# Revit family: Door-Exterior_Interior-Simpson-French-Full_Glass-Half_Arch-Single
name_source: partatom
category: Doors
revit_build: Autodesk Revit Architecture 2012 (Build: 20110916_2132(x64)
units: mm (PartAtom-declared; Revit-internal decimal feet)

## types (231) — shared parameters
Arch Bottom Height = 0' - 9 13/32"
Assembly Code = B2030230
Bottom Rail Height = 0' - 8 13/16"
Construction Type = Wood
Frame = Wood - Simpson Doors - Douglas Fir
Frame Projection Ext. = 0' - 1"
Frame Projection Int. = 0' - 1"
Frame Type = Frame : Standard
Frame Width = 0' - 3"
Function = Exterior
Glass = Glass - Simpson Doors - Clear
Glass Options = http://simpsondoor.com
Manufacturer = Simpsons Door Company
Middle Rail Height = 0' - 6 3/4"
Muntin Width = 0' - 0 1/2"
Ovolo Construction = Yes
Panel = Wood - Simpson Doors - Douglas Fir
Panel Stile Width = 0' - 4 1/8"
Product Documentation Link = http://www.simpsondoor.com
Product Page URL = http://www.simpsondoor.com
Thickness = 0' - 1 3/4"
Thickness Note = comes in 1 3/4" and 2 1/4" Thickness. Default is set to 1 3/4"
Top Rail Height = 0' - 4 1/32"
URL = http://www.simpsondoor.com
UltraBlock Note = This Door Comes with The Option of UltraBlock Technology. It is Turn On as a Default
UltraBlock Option = Yes
Wall Closure = By host
WaterBarrier Note = This Door Comes with The Option of WaterBarrier with UltraBlock Technology. It is Turn Off as a Default
WaterBarrier with UltraBlock Technology = No
Wood Species = http://simpsondoor.com
Wood Species Note = Available in Any Wood Species

## per-type parameters (varying)
| type | Description | Height | Model | Number of Horizontal Muntins | Number of Vertical Muntins | Rough Height | Rough Width | Width |
| 1420-1430 Exterior French 30x80 Ovolo Flat Panel | Exterior French - Ten Lite | 6' - 8" | 1420-1430 | 4 | 1 | 6' - 10" | 2' - 10" | 2' - 6" |
| 1420-1430 Exterior French 30x84 Ovolo Flat Panel | Exterior French - Ten Lite | 7' - 0" | 1420-1430 | 4 | 1 | 7' - 2" | 2' - 10" | 2' - 6" |
| 1420-1430 Exterior French 30x96 Ovolo Flat Panel | Exterior French - Ten Lite | 8' - 0" | 1420-1430 | 4 | 1 | 8' - 2" | 2' - 10" | 2' - 6" |
| 1420-1430 Exterior French 32x80 Ovolo Flat Panel | Exterior French - Ten Lite | 6' - 8" | 1420-1430 | 4 | 1 | 6' - 10" | 3' - 0" | 2' - 8" |
| 1420-1430 Exterior French 32x84 Ovolo Flat Panel | Exterior French - Ten Lite | 7' - 0" | 1420-1430 | 4 | 1 | 7' - 2" | 3' - 0" | 2' - 8" |
| 1420-1430 Exterior French 32x96 Ovolo Flat Panel | Exterior French - Ten Lite | 8' - 0" | 1420-1430 | 4 | 1 | 8' - 2" | 3' - 0" | 2' - 8" |
| 1420-1430 Exterior French 34x80 Ovolo Flat Panel | Exterior French - Ten Lite | 6' - 8" | 1420-1430 | 4 | 1 | 6' - 10" | 3' - 2" | 2' - 10" |
| 1420-1430 Exterior French 34x84 Ovolo Flat Panel | Exterior French - Ten Lite | 7' - 0" | 1420-1430 | 4 | 1 | 7' - 2" | 3' - 2" | 2' - 10" |
| 1420-1430 Exterior French 34x96 Ovolo Flat Panel | Exterior French - Ten Lite | 8' - 0" | 1420-1430 | 4 | 1 | 8' - 2" | 3' - 2" | 2' - 10" |
| 1420-1430 Exterior French 36x80 Ovolo Flat Panel | Exterior French - Ten Lite | 6' - 8" | 1420-1430 | 4 | 1 | 6' - 10" | 3' - 4" | 3' - 0" |
| 1420-1430 Exterior French 36x84 Ovolo Flat Panel | Exterior French - Ten Lite | 7' - 0" | 1420-1430 | 4 | 1 | 7' - 2" | 3' - 4" | 3' - 0" |
| 1420-1430 Exterior French 36x96 Ovolo Flat Panel | Exterior French - Ten Lite | 8' - 0" | 1420-1430 | 4 | 1 | 8' - 2" | 3' - 4" | 3' - 0" |
| 1420-1430 Exterior French 38x80 Ovolo Flat Panel | Exterior French - Ten Lite | 6' - 8" | 1420-1430 | 4 | 1 | 6' - 10" | 3' - 6" | 3' - 2" |
| 1420-1430 Exterior French 38x84 Ovolo Flat Panel | Exterior French - Ten Lite | 7' - 0" | 1420-1430 | 4 | 1 | 7' - 2" | 3' - 6" | 3' - 2" |
| 1420-1430 Exterior French 38x96 Ovolo Flat Panel | Exterior French - Ten Lite | 8' - 0" | 1420-1430 | 4 | 1 | 8' - 2" | 3' - 6" | 3' - 2" |
| 1420-1430 Exterior French 40x80 Ovolo Flat Panel | Exterior French - Ten Lite | 6' - 8" | 1420-1430 | 4 | 1 | 6' - 10" | 3' - 8" | 3' - 4" |
| 1420-1430 Exterior French 40x84 Ovolo Flat Panel | Exterior French - Ten Lite | 7' - 0" | 1420-1430 | 4 | 1 | 7' - 2" | 3' - 8" | 3' - 4" |
| 1420-1430 Exterior French 40x96 Ovolo Flat Panel | Exterior French - Ten Lite | 8' - 0" | 1420-1430 | 4 | 1 | 8' - 2" | 3' - 8" | 3' - 4" |
| 1420-1430 Exterior French 42x80 Ovolo Flat Panel | Exterior French - Ten Lite | 6' - 8" | 1420-1430 | 4 | 1 | 6' - 10" | 3' - 10" | 3' - 6" |
| 1420-1430 Exterior French 42x84 Ovolo Flat Panel | Exterior French - Ten Lite | 7' - 0" | 1420-1430 | 4 | 1 | 7' - 2" | 3' - 10" | 3' - 6" |
| 1420-1430 Exterior French 42x96 Ovolo Flat Panel | Exterior French - Ten Lite | 8' - 0" | 1420-1430 | 4 | 1 | 8' - 2" | 3' - 10" | 3' - 6" |
| 1421-1431 Exterior French 30x80 Ovolo Flat Panel | Exterior French - Single Lite | 6' - 8" | 1421-1431 | 0 | 0 | 6' - 10" | 2' - 10" | 2' - 6" |
| 1421-1431 Exterior French 30x84 Ovolo Flat Panel | Exterior French - Single Lite | 7' - 0" | 1421-1431 | 0 | 0 | 7' - 2" | 2' - 10" | 2' - 6" |
| 1421-1431 Exterior French 30x96 Ovolo Flat Panel | Exterior French - Single Lite | 8' - 0" | 1421-1431 | 0 | 0 | 8' - 2" | 2' - 10" | 2' - 6" |
| 1421-1431 Exterior French 32x80 Ovolo Flat Panel | Exterior French - Single Lite | 6' - 8" | 1421-1431 | 0 | 0 | 6' - 10" | 3' - 0" | 2' - 8" |
| 1421-1431 Exterior French 32x84 Ovolo Flat Panel | Exterior French - Single Lite | 7' - 0" | 1421-1431 | 0 | 0 | 7' - 2" | 3' - 0" | 2' - 8" |
| 1421-1431 Exterior French 32x96 Ovolo Flat Panel | Exterior French - Single Lite | 8' - 0" | 1421-1431 | 0 | 0 | 8' - 2" | 3' - 0" | 2' - 8" |
| 1421-1431 Exterior French 34x80 Ovolo Flat Panel | Exterior French - Single Lite | 6' - 8" | 1421-1431 | 0 | 0 | 6' - 10" | 3' - 2" | 2' - 10" |
| 1421-1431 Exterior French 34x84 Ovolo Flat Panel | Exterior French - Single Lite | 7' - 0" | 1421-1431 | 0 | 0 | 7' - 2" | 3' - 2" | 2' - 10" |
| 1421-1431 Exterior French 34x96 Ovolo Flat Panel | Exterior French - Single Lite | 8' - 0" | 1421-1431 | 0 | 0 | 8' - 2" | 3' - 2" | 2' - 10" |
| 1421-1431 Exterior French 36x80 Ovolo Flat Panel | Exterior French - Single Lite | 6' - 8" | 1421-1431 | 0 | 0 | 6' - 10" | 3' - 4" | 3' - 0" |
| 1421-1431 Exterior French 36x84 Ovolo Flat Panel | Exterior French - Single Lite | 7' - 0" | 1421-1431 | 0 | 0 | 7' - 2" | 3' - 4" | 3' - 0" |
| 1421-1431 Exterior French 36x96 Ovolo Flat Panel | Exterior French - Single Lite | 8' - 0" | 1421-1431 | 0 | 0 | 8' - 2" | 3' - 4" | 3' - 0" |
| 1421-1431 Exterior French 38x80 Ovolo Flat Panel | Exterior French - Single Lite | 6' - 8" | 1421-1431 | 0 | 0 | 6' - 10" | 3' - 6" | 3' - 2" |
| 1421-1431 Exterior French 38x84 Ovolo Flat Panel | Exterior French - Single Lite | 7' - 0" | 1421-1431 | 0 | 0 | 7' - 2" | 3' - 6" | 3' - 2" |
| 1421-1431 Exterior French 38x96 Ovolo Flat Panel | Exterior French - Single Lite | 8' - 0" | 1421-1431 | 0 | 0 | 8' - 2" | 3' - 6" | 3' - 2" |
| 1421-1431 Exterior French 40x80 Ovolo Flat Panel | Exterior French - Single Lite | 6' - 8" | 1421-1431 | 0 | 0 | 6' - 10" | 3' - 8" | 3' - 4" |
| 1421-1431 Exterior French 40x84 Ovolo Flat Panel | Exterior French - Single Lite | 7' - 0" | 1421-1431 | 0 | 0 | 7' - 2" | 3' - 8" | 3' - 4" |
| 1421-1431 Exterior French 40x96 Ovolo Flat Panel | Exterior French - Single Lite | 8' - 0" | 1421-1431 | 0 | 0 | 8' - 2" | 3' - 8" | 3' - 4" |
| 1421-1431 Exterior French 42x80 Ovolo Flat Panel | Exterior French - Single Lite | 6' - 8" | 1421-1431 | 0 | 0 | 6' - 10" | 3' - 10" | 3' - 6" |
| 1421-1431 Exterior French 42x84 Ovolo Flat Panel | Exterior French - Single Lite | 7' - 0" | 1421-1431 | 0 | 0 | 7' - 2" | 3' - 10" | 3' - 6" |
| 1421-1431 Exterior French 42x96 Ovolo Flat Panel | Exterior French - Single Lite | 8' - 0" | 1421-1431 | 0 | 0 | 8' - 2" | 3' - 10" | 3' - 6" |
| 1426 -1436 Exterior French 30x80 Ovolo Flat Panel | Exterior French - Six Lite | 6' - 8" | 1426-1436 | 2 | 1 | 6' - 10" | 2' - 10" | 2' - 6" |
| 1426-1436 Exterior French 30x84 Ovolo Flat Panel | Exterior French - Six Lite | 7' - 0" | 1426-1436 | 2 | 1 | 7' - 2" | 2' - 10" | 2' - 6" |
| 1426-1436 Exterior French 30x96 Ovolo Flat Panel | Exterior French - Six Lite | 8' - 0" | 1426-1436 | 2 | 1 | 8' - 2" | 2' - 10" | 2' - 6" |
| 1426-1436 Exterior French 32x80 Ovolo Flat Panel | Exterior French - Six Lite | 6' - 8" | 1426-1436 | 2 | 1 | 6' - 10" | 3' - 0" | 2' - 8" |
| 1426-1436 Exterior French 32x84 Ovolo Flat Panel | Exterior French - Six Lite | 7' - 0" | 1426-1436 | 2 | 1 | 7' - 2" | 3' - 0" | 2' - 8" |
| 1426-1436 Exterior French 32x96 Ovolo Flat Panel | Exterior French - Six Lite | 8' - 0" | 1426-1436 | 2 | 1 | 8' - 2" | 3' - 0" | 2' - 8" |
| 1426-1436 Exterior French 34x80 Ovolo Flat Panel | Exterior French - Six Lite | 6' - 8" | 1426-1436 | 2 | 1 | 6' - 10" | 3' - 2" | 2' - 10" |
| 1426-1436 Exterior French 34x84 Ovolo Flat Panel | Exterior French - Six Lite | 7' - 0" | 1426-1436 | 2 | 1 | 7' - 2" | 3' - 2" | 2' - 10" |
| 1426-1436 Exterior French 34x96 Ovolo Flat Panel | Exterior French - Six Lite | 8' - 0" | 1426-1436 | 2 | 1 | 8' - 2" | 3' - 2" | 2' - 10" |
| 1426-1436 Exterior French 36x80 Ovolo Flat Panel | Exterior French - Six Lite | 6' - 8" | 1426-1436 | 2 | 1 | 6' - 10" | 3' - 4" | 3' - 0" |
| 1426-1436 Exterior French 36x84 Ovolo Flat Panel | Exterior French - Six Lite | 7' - 0" | 1426-1436 | 2 | 1 | 7' - 2" | 3' - 4" | 3' - 0" |
| 1426-1436 Exterior French 36x96 Ovolo Flat Panel | Exterior French - Six Lite | 8' - 0" | 1426-1436 | 2 | 1 | 8' - 2" | 3' - 4" | 3' - 0" |
| 1426-1436 Exterior French 38x80 Ovolo Flat Panel | Exterior French - Six Lite | 6' - 8" | 1426-1436 | 2 | 1 | 6' - 10" | 3' - 6" | 3' - 2" |
| 1426-1436 Exterior French 38x84 Ovolo Flat Panel | Exterior French - Six Lite | 7' - 0" | 1426-1436 | 2 | 1 | 7' - 2" | 3' - 6" | 3' - 2" |
| 1426-1436 Exterior French 38x96 Ovolo Flat Panel | Exterior French - Six Lite | 8' - 0" | 1426-1436 | 2 | 1 | 8' - 2" | 3' - 6" | 3' - 2" |
| 1426-1436 Exterior French 40x80 Ovolo Flat Panel | Exterior French - Six Lite | 6' - 8" | 1426-1436 | 2 | 1 | 6' - 10" | 3' - 8" | 3' - 4" |
| 1426-1436 Exterior French 40x84 Ovolo Flat Panel | Exterior French - Six Lite | 7' - 0" | 1426-1436 | 2 | 1 | 7' - 2" | 3' - 8" | 3' - 4" |
| 1426-1436 Exterior French 40x96 Ovolo Flat Panel | Exterior French - Six Lite | 8' - 0" | 1426-1436 | 2 | 1 | 8' - 2" | 3' - 8" | 3' - 4" |
| 1426-1436 Exterior French 42x80 Ovolo Flat Panel | Exterior French - Six Lite | 6' - 8" | 1426-1436 | 2 | 1 | 6' - 10" | 3' - 10" | 3' - 6" |
| 1426-1436 Exterior French 42x84 Ovolo Flat Panel | Exterior French - Six Lite | 7' - 0" | 1426-1436 | 2 | 1 | 7' - 2" | 3' - 10" | 3' - 6" |
| 1426-1436 Exterior French 42x96 Ovolo Flat Panel | Exterior French - Six Lite | 8' - 0" | 1426-1436 | 2 | 1 | 8' - 2" | 3' - 10" | 3' - 6" |
| 1428 -1438 Exterior French 30x80 Ovolo Flat Panel | Exterior French - Eight Lite | 6' - 8" | 1428-1438 | 3 | 1 | 6' - 10" | 2' - 10" | 2' - 6" |
| 1428-1438 Exterior French 30x84 Ovolo Flat Panel | Exterior French - Eight Lite | 7' - 0" | 1428-1438 | 3 | 1 | 7' - 2" | 2' - 10" | 2' - 6" |
| 1428-1438 Exterior French 30x96 Ovolo Flat Panel | Exterior French - Eight Lite | 8' - 0" | 1428-1438 | 3 | 1 | 8' - 2" | 2' - 10" | 2' - 6" |
| 1428-1438 Exterior French 32x80 Ovolo Flat Panel | Exterior French - Eight Lite | 6' - 8" | 1428-1438 | 3 | 1 | 6' - 10" | 3' - 0" | 2' - 8" |
| 1428-1438 Exterior French 32x84 Ovolo Flat Panel | Exterior French - Eight Lite | 7' - 0" | 1428-1438 | 3 | 1 | 7' - 2" | 3' - 0" | 2' - 8" |
| 1428-1438 Exterior French 32x96 Ovolo Flat Panel | Exterior French - Eight Lite | 8' - 0" | 1428-1438 | 3 | 1 | 8' - 2" | 3' - 0" | 2' - 8" |
| 1428-1438 Exterior French 34x80 Ovolo Flat Panel | Exterior French - Eight Lite | 6' - 8" | 1428-1438 | 3 | 1 | 6' - 10" | 3' - 2" | 2' - 10" |
| 1428-1438 Exterior French 34x84 Ovolo Flat Panel | Exterior French - Eight Lite | 7' - 0" | 1428-1438 | 3 | 1 | 7' - 2" | 3' - 2" | 2' - 10" |
| 1428-1438 Exterior French 34x96 Ovolo Flat Panel | Exterior French - Eight Lite | 8' - 0" | 1428-1438 | 3 | 1 | 8' - 2" | 3' - 2" | 2' - 10" |
| 1428-1438 Exterior French 36x80 Ovolo Flat Panel | Exterior French - Eight Lite | 6' - 8" | 1428-1438 | 3 | 1 | 6' - 10" | 3' - 4" | 3' - 0" |
| 1428-1438 Exterior French 36x84 Ovolo Flat Panel | Exterior French - Eight Lite | 7' - 0" | 1428-1438 | 3 | 1 | 7' - 2" | 3' - 4" | 3' - 0" |
| 1428-1438 Exterior French 36x96 Ovolo Flat Panel | Exterior French - Eight Lite | 8' - 0" | 1428-1438 | 3 | 1 | 8' - 2" | 3' - 4" | 3' - 0" |
| 1428-1438 Exterior French 38x80 Ovolo Flat Panel | Exterior French - Eight Lite | 6' - 8" | 1428-1438 | 3 | 1 | 6' - 10" | 3' - 6" | 3' - 2" |
| 1428-1438 Exterior French 38x84 Ovolo Flat Panel | Exterior French - Eight Lite | 7' - 0" | 1428-1438 | 3 | 1 | 7' - 2" | 3' - 6" | 3' - 2" |
| 1428-1438 Exterior French 38x96 Ovolo Flat Panel | Exterior French - Eight Lite | 8' - 0" | 1428-1438 | 3 | 1 | 8' - 2" | 3' - 6" | 3' - 2" |
| 1428-1438 Exterior French 40x80 Ovolo Flat Panel | Exterior French - Eight Lite | 6' - 8" | 1428-1438 | 3 | 1 | 6' - 10" | 3' - 8" | 3' - 4" |
| 1428-1438 Exterior French 40x84 Ovolo Flat Panel | Exterior French - Eight Lite | 7' - 0" | 1428-1438 | 3 | 1 | 7' - 2" | 3' - 8" | 3' - 4" |
| 1428-1438 Exterior French 40x96 Ovolo Flat Panel | Exterior French - Eight Lite | 8' - 0" | 1428-1438 | 3 | 1 | 8' - 2" | 3' - 8" | 3' - 4" |
| 1428-1438 Exterior French 42x80 Ovolo Flat Panel | Exterior French - Eight Lite | 6' - 8" | 1428-1438 | 3 | 1 | 6' - 10" | 3' - 10" | 3' - 6" |
| 1428-1438 Exterior French 42x84 Ovolo Flat Panel | Exterior French - Eight Lite | 7' - 0" | 1428-1438 | 3 | 1 | 7' - 2" | 3' - 10" | 3' - 6" |
| 1428-1438 Exterior French 42x96 Ovolo Flat Panel | Exterior French - Eight Lite | 8' - 0" | 1428-1438 | 3 | 1 | 8' - 2" | 3' - 10" | 3' - 6" |
| 37170-37180 Thermal French 30x80 Ovolo Flat Panel | Thermal French SDL - Single Lite - Insulated Glazed | 6' - 8" | 37170-37180 | 4 | 1 | 6' - 10" | 2' - 10" | 2' - 6" |
| 37170-37180 Thermal French 30x84 Ovolo Flat Panel | Thermal French SDL - Single Lite - Insulated Glazed | 7' - 0" | 37170-37180 | 4 | 1 | 7' - 2" | 2' - 10" | 2' - 6" |
| 37170-37180 Thermal French 30x96 Ovolo Flat Panel | Thermal French SDL - Single Lite - Insulated Glazed | 8' - 0" | 37170-37180 | 4 | 1 | 8' - 2" | 2' - 10" | 2' - 6" |
| 37170-37180 Thermal French 32x80 Ovolo Flat Panel | Thermal French SDL - Single Lite - Insulated Glazed | 6' - 8" | 37170-37180 | 4 | 1 | 6' - 10" | 3' - 0" | 2' - 8" |
| 37170-37180 Thermal French 32x84 Ovolo Flat Panel | Thermal French SDL - Single Lite - Insulated Glazed | 7' - 0" | 37170-37180 | 4 | 1 | 7' - 2" | 3' - 0" | 2' - 8" |
| 37170-37180 Thermal French 32x96 Ovolo Flat Panel | Thermal French SDL - Single Lite - Insulated Glazed | 8' - 0" | 37170-37180 | 4 | 1 | 8' - 2" | 3' - 0" | 2' - 8" |
| 37170-37180 Thermal French 34x80 Ovolo Flat Panel | Thermal French SDL - Single Lite - Insulated Glazed | 6' - 8" | 37170-37180 | 4 | 1 | 6' - 10" | 3' - 2" | 2' - 10" |
| 37170-37180 Thermal French 34x84 Ovolo Flat Panel | Thermal French SDL - Single Lite - Insulated Glazed | 7' - 0" | 37170-37180 | 4 | 1 | 7' - 2" | 3' - 2" | 2' - 10" |
| 37170-37180 Thermal French 34x96 Ovolo Flat Panel | Thermal French SDL - Single Lite - Insulated Glazed | 8' - 0" | 37170-37180 | 4 | 1 | 8' - 2" | 3' - 2" | 2' - 10" |
| 37170-37180 Thermal French 36x80 Ovolo Flat Panel | Thermal French SDL - Single Lite - Insulated Glazed | 6' - 8" | 37170-37180 | 4 | 1 | 6' - 10" | 3' - 4" | 3' - 0" |
| 37170-37180 Thermal French 36x84 Ovolo Flat Panel | Thermal French SDL - Single Lite - Insulated Glazed | 7' - 0" | 37170-37180 | 4 | 1 | 7' - 2" | 3' - 4" | 3' - 0" |
| 37170-37180 Thermal French 36x96 Ovolo Flat Panel | Thermal French SDL - Single Lite - Insulated Glazed | 8' - 0" | 37170-37180 | 4 | 1 | 8' - 2" | 3' - 4" | 3' - 0" |
| 37170-37180 Thermal French 38x80 Ovolo Flat Panel | Thermal French SDL - Single Lite - Insulated Glazed | 6' - 8" | 37170-37180 | 4 | 1 | 6' - 10" | 3' - 6" | 3' - 2" |
| 37170-37180 Thermal French 38x84 Ovolo Flat Panel | Thermal French SDL - Single Lite - Insulated Glazed | 7' - 0" | 37170-37180 | 4 | 1 | 7' - 2" | 3' - 6" | 3' - 2" |
| 37170-37180 Thermal French 38x96 Ovolo Flat Panel | Thermal French SDL - Single Lite - Insulated Glazed | 8' - 0" | 37170-37180 | 4 | 1 | 8' - 2" | 3' - 6" | 3' - 2" |
| 37170-37180 Thermal French 40x80 Ovolo Flat Panel | Thermal French SDL - Single Lite - Insulated Glazed | 6' - 8" | 37170-37180 | 4 | 1 | 6' - 10" | 3' - 8" | 3' - 4" |
| 37170-37180 Thermal French 40x84 Ovolo Flat Panel | Thermal French SDL - Single Lite - Insulated Glazed | 7' - 0" | 37170-37180 | 4 | 1 | 7' - 2" | 3' - 8" | 3' - 4" |
| 37170-37180 Thermal French 40x96 Ovolo Flat Panel | Thermal French SDL - Single Lite - Insulated Glazed | 8' - 0" | 37170-37180 | 4 | 1 | 8' - 2" | 3' - 8" | 3' - 4" |
| 37170-37180 Thermal French 42x80 Ovolo Flat Panel | Thermal French SDL - Single Lite - Insulated Glazed | 6' - 8" | 37170-37180 | 4 | 1 | 6' - 10" | 3' - 10" | 3' - 6" |
| 37170-37180 Thermal French 42x84 Ovolo Flat Panel | Thermal French SDL - Single Lite - Insulated Glazed | 7' - 0" | 37170-37180 | 4 | 1 | 7' - 2" | 3' - 10" | 3' - 6" |
| 37170-37180 Thermal French 42x96 Ovolo Flat Panel | Thermal French SDL - Single Lite - Insulated Glazed | 8' - 0" | 37170-37180 | 4 | 1 | 8' - 2" | 3' - 10" | 3' - 6" |
| 37176-37186 Thermal French 30x80 Ovolo Flat Panel | Thermal French SDL - Six Lite | 6' - 8" | 37176-37186 | 2 | 1 | 6' - 10" | 2' - 10" | 2' - 6" |
| 37176-37186 Thermal French 30x84 Ovolo Flat Panel | Thermal French SDL - Six Lite | 7' - 0" | 37176-37186 | 2 | 1 | 7' - 2" | 2' - 10" | 2' - 6" |
| 37176-37186 Thermal French 30x96 Ovolo Flat Panel | Thermal French SDL - Six Lite | 8' - 0" | 37176-37186 | 2 | 1 | 8' - 2" | 2' - 10" | 2' - 6" |
| 37176-37186 Thermal French 32x80 Ovolo Flat Panel | Thermal French SDL - Six Lite | 6' - 8" | 37176-37186 | 2 | 1 | 6' - 10" | 3' - 0" | 2' - 8" |
| 37176-37186 Thermal French 32x84 Ovolo Flat Panel | Thermal French SDL - Six Lite | 7' - 0" | 37176-37186 | 2 | 1 | 7' - 2" | 3' - 0" | 2' - 8" |
| 37176-37186 Thermal French 32x96 Ovolo Flat Panel | Thermal French SDL - Six Lite | 8' - 0" | 37176-37186 | 2 | 1 | 8' - 2" | 3' - 0" | 2' - 8" |
| 37176-37186 Thermal French 34x80 Ovolo Flat Panel | Thermal French SDL - Six Lite | 6' - 8" | 37176-37186 | 2 | 1 | 6' - 10" | 3' - 2" | 2' - 10" |
| 37176-37186 Thermal French 34x84 Ovolo Flat Panel | Thermal French SDL - Six Lite | 7' - 0" | 37176-37186 | 2 | 1 | 7' - 2" | 3' - 2" | 2' - 10" |
| 37176-37186 Thermal French 34x96 Ovolo Flat Panel | Thermal French SDL - Six Lite | 8' - 0" | 37176-37186 | 2 | 1 | 8' - 2" | 3' - 2" | 2' - 10" |
| 37176-37186 Thermal French 36x80 Ovolo Flat Panel | Thermal French SDL - Six Lite | 6' - 8" | 37176-37186 | 2 | 1 | 6' - 10" | 3' - 4" | 3' - 0" |
| 37176-37186 Thermal French 36x84 Ovolo Flat Panel | Thermal French SDL - Six Lite | 7' - 0" | 37176-37186 | 2 | 1 | 7' - 2" | 3' - 4" | 3' - 0" |
| 37176-37186 Thermal French 36x96 Ovolo Flat Panel | Thermal French SDL - Six Lite | 8' - 0" | 37176-37186 | 2 | 1 | 8' - 2" | 3' - 4" | 3' - 0" |
| 37176-37186 Thermal French 38x80 Ovolo Flat Panel | Thermal French SDL - Six Lite | 6' - 8" | 37176-37186 | 2 | 1 | 6' - 10" | 3' - 6" | 3' - 2" |
| 37176-37186 Thermal French 38x84 Ovolo Flat Panel | Thermal French SDL - Six Lite | 7' - 0" | 37176-37186 | 2 | 1 | 7' - 2" | 3' - 6" | 3' - 2" |
| 37176-37186 Thermal French 38x96 Ovolo Flat Panel | Thermal French SDL - Six Lite | 8' - 0" | 37176-37186 | 2 | 1 | 8' - 2" | 3' - 6" | 3' - 2" |
| 37176-37186 Thermal French 40x80 Ovolo Flat Panel | Thermal French SDL - Six Lite | 6' - 8" | 37176-37186 | 2 | 1 | 6' - 10" | 3' - 8" | 3' - 4" |
| 37176-37186 Thermal French 40x84 Ovolo Flat Panel | Thermal French SDL - Six Lite | 7' - 0" | 37176-37186 | 2 | 1 | 7' - 2" | 3' - 8" | 3' - 4" |
| 37176-37186 Thermal French 40x96 Ovolo Flat Panel | Thermal French SDL - Six Lite | 8' - 0" | 37176-37186 | 2 | 1 | 8' - 2" | 3' - 8" | 3' - 4" |
| 37176-37186 Thermal French 42x80 Ovolo Flat Panel | Thermal French SDL - Six Lite | 6' - 8" | 37176-37186 | 2 | 1 | 6' - 10" | 3' - 10" | 3' - 6" |
| 37176-37186 Thermal French 42x84 Ovolo Flat Panel | Thermal French SDL - Six Lite | 7' - 0" | 37176-37186 | 2 | 1 | 7' - 2" | 3' - 10" | 3' - 6" |
| 37176-37186 Thermal French 42x96 Ovolo Flat Panel | Thermal French SDL - Six Lite | 8' - 0" | 37176-37186 | 2 | 1 | 8' - 2" | 3' - 10" | 3' - 6" |
| 37178-37188 Thermal French 30x80 Ovolo Flat Panel | Thermal French SDL - Eight Lite | 6' - 8" | 37178-37188 | 3 | 1 | 6' - 10" | 2' - 10" | 2' - 6" |
| 37178-37188 Thermal French 30x84 Ovolo Flat Panel | Thermal French SDL - Eight Lite | 7' - 0" | 37178-37188 | 3 | 1 | 7' - 2" | 2' - 10" | 2' - 6" |
| 37178-37188 Thermal French 30x96 Ovolo Flat Panel | Thermal French SDL - Eight Lite | 8' - 0" | 37178-37188 | 3 | 1 | 8' - 2" | 2' - 10" | 2' - 6" |
| 37178-37188 Thermal French 32x80 Ovolo Flat Panel | Thermal French SDL - Eight Lite | 6' - 8" | 37178-37188 | 3 | 1 | 6' - 10" | 3' - 0" | 2' - 8" |
| 37178-37188 Thermal French 32x84 Ovolo Flat Panel | Thermal French SDL - Eight Lite | 7' - 0" | 37178-37188 | 3 | 1 | 7' - 2" | 3' - 0" | 2' - 8" |
| 37178-37188 Thermal French 32x96 Ovolo Flat Panel | Thermal French SDL - Eight Lite | 8' - 0" | 37178-37188 | 3 | 1 | 8' - 2" | 3' - 0" | 2' - 8" |
| 37178-37188 Thermal French 34x80 Ovolo Flat Panel | Thermal French SDL - Eight Lite | 6' - 8" | 37178-37188 | 3 | 1 | 6' - 10" | 3' - 2" | 2' - 10" |
| 37178-37188 Thermal French 34x84 Ovolo Flat Panel | Thermal French SDL - Eight Lite | 7' - 0" | 37178-37188 | 3 | 1 | 7' - 2" | 3' - 2" | 2' - 10" |
| 37178-37188 Thermal French 34x96 Ovolo Flat Panel | Thermal French SDL - Eight Lite | 8' - 0" | 37178-37188 | 3 | 1 | 8' - 2" | 3' - 2" | 2' - 10" |
| 37178-37188 Thermal French 36x80 Ovolo Flat Panel | Thermal French SDL - Eight Lite | 6' - 8" | 37178-37188 | 3 | 1 | 6' - 10" | 3' - 4" | 3' - 0" |
| 37178-37188 Thermal French 36x84 Ovolo Flat Panel | Thermal French SDL - Eight Lite | 7' - 0" | 37178-37188 | 3 | 1 | 7' - 2" | 3' - 4" | 3' - 0" |
| 37178-37188 Thermal French 36x96 Ovolo Flat Panel | Thermal French SDL - Eight Lite | 8' - 0" | 37178-37188 | 3 | 1 | 8' - 2" | 3' - 4" | 3' - 0" |
| 37178-37188 Thermal French 38x80 Ovolo Flat Panel | Thermal French SDL - Eight Lite | 6' - 8" | 37178-37188 | 3 | 1 | 6' - 10" | 3' - 6" | 3' - 2" |
| 37178-37188 Thermal French 38x84 Ovolo Flat Panel | Thermal French SDL - Eight Lite | 7' - 0" | 37178-37188 | 3 | 1 | 7' - 2" | 3' - 6" | 3' - 2" |
| 37178-37188 Thermal French 38x96 Ovolo Flat Panel | Thermal French SDL - Eight Lite | 8' - 0" | 37178-37188 | 3 | 1 | 8' - 2" | 3' - 6" | 3' - 2" |
| 37178-37188 Thermal French 40x80 Ovolo Flat Panel | Thermal French SDL - Eight Lite | 6' - 8" | 37178-37188 | 3 | 1 | 6' - 10" | 3' - 8" | 3' - 4" |
| 37178-37188 Thermal French 40x84 Ovolo Flat Panel | Thermal French SDL - Eight Lite | 7' - 0" | 37178-37188 | 3 | 1 | 7' - 2" | 3' - 8" | 3' - 4" |
| 37178-37188 Thermal French 40x96 Ovolo Flat Panel | Thermal French SDL - Eight Lite | 8' - 0" | 37178-37188 | 3 | 1 | 8' - 2" | 3' - 8" | 3' - 4" |
| 37178-37188 Thermal French 42x80 Ovolo Flat Panel | Thermal French SDL - Eight Lite | 6' - 8" | 37178-37188 | 3 | 1 | 6' - 10" | 3' - 10" | 3' - 6" |
| 37178-37188 Thermal French 42x84 Ovolo Flat Panel | Thermal French SDL - Eight Lite | 7' - 0" | 37178-37188 | 3 | 1 | 7' - 2" | 3' - 10" | 3' - 6" |
| 37178-37188 Thermal French 42x96 Ovolo Flat Panel | Thermal French SDL - Eight Lite | 8' - 0" | 37178-37188 | 3 | 1 | 8' - 2" | 3' - 10" | 3' - 6" |
| 7170-7180 Thermal French 30x80 Ovolo Flat Panel | Thermal French TDL - Single Lite - Insulated Glazed | 6' - 8" | 7170-7180 | 4 | 1 | 6' - 10" | 2' - 10" | 2' - 6" |
| 7170-7180 Thermal French 30x84 Ovolo Flat Panel | Thermal French TDL - Single Lite - Insulated Glazed | 7' - 0" | 7170-7180 | 4 | 1 | 7' - 2" | 2' - 10" | 2' - 6" |
| 7170-7180 Thermal French 30x96 Ovolo Flat Panel | Thermal French TDL - Single Lite - Insulated Glazed | 8' - 0" | 7170-7180 | 4 | 1 | 8' - 2" | 2' - 10" | 2' - 6" |
| 7170-7180 Thermal French 32x80 Ovolo Flat Panel | Thermal French TDL - Single Lite - Insulated Glazed | 6' - 8" | 7170-7180 | 4 | 1 | 6' - 10" | 3' - 0" | 2' - 8" |
| 7170-7180 Thermal French 32x84 Ovolo Flat Panel | Thermal French TDL - Single Lite - Insulated Glazed | 7' - 0" | 7170-7180 | 4 | 1 | 7' - 2" | 3' - 0" | 2' - 8" |
| 7170-7180 Thermal French 32x96 Ovolo Flat Panel | Thermal French TDL - Single Lite - Insulated Glazed | 8' - 0" | 7170-7180 | 4 | 1 | 8' - 2" | 3' - 0" | 2' - 8" |
| 7170-7180 Thermal French 34x80 Ovolo Flat Panel | Thermal French TDL - Single Lite - Insulated Glazed | 6' - 8" | 7170-7180 | 4 | 1 | 6' - 10" | 3' - 2" | 2' - 10" |
| 7170-7180 Thermal French 34x84 Ovolo Flat Panel | Thermal French TDL - Single Lite - Insulated Glazed | 7' - 0" | 7170-7180 | 4 | 1 | 7' - 2" | 3' - 2" | 2' - 10" |
| 7170-7180 Thermal French 34x96 Ovolo Flat Panel | Thermal French TDL - Single Lite - Insulated Glazed | 8' - 0" | 7170-7180 | 4 | 1 | 8' - 2" | 3' - 2" | 2' - 10" |
| 7170-7180 Thermal French 36x80 Ovolo Flat Panel | Thermal French TDL - Single Lite - Insulated Glazed | 6' - 8" | 7170-7180 | 4 | 1 | 6' - 10" | 3' - 4" | 3' - 0" |
| 7170-7180 Thermal French 36x84 Ovolo Flat Panel | Thermal French TDL - Single Lite - Insulated Glazed | 7' - 0" | 7170-7180 | 4 | 1 | 7' - 2" | 3' - 4" | 3' - 0" |
| 7170-7180 Thermal French 36x96 Ovolo Flat Panel | Thermal French TDL - Single Lite - Insulated Glazed | 8' - 0" | 7170-7180 | 4 | 1 | 8' - 2" | 3' - 4" | 3' - 0" |
| 7170-7180 Thermal French 38x80 Ovolo Flat Panel | Thermal French TDL - Single Lite - Insulated Glazed | 6' - 8" | 7170-7180 | 4 | 1 | 6' - 10" | 3' - 6" | 3' - 2" |
| 7170-7180 Thermal French 38x84 Ovolo Flat Panel | Thermal French TDL - Single Lite - Insulated Glazed | 7' - 0" | 7170-7180 | 4 | 1 | 7' - 2" | 3' - 6" | 3' - 2" |
| 7170-7180 Thermal French 38x96 Ovolo Flat Panel | Thermal French TDL - Single Lite - Insulated Glazed | 8' - 0" | 7170-7180 | 4 | 1 | 8' - 2" | 3' - 6" | 3' - 2" |
| 7170-7180 Thermal French 40x80 Ovolo Flat Panel | Thermal French TDL - Single Lite - Insulated Glazed | 6' - 8" | 7170-7180 | 4 | 1 | 6' - 10" | 3' - 8" | 3' - 4" |
| 7170-7180 Thermal French 40x84 Ovolo Flat Panel | Thermal French TDL - Single Lite - Insulated Glazed | 7' - 0" | 7170-7180 | 4 | 1 | 7' - 2" | 3' - 8" | 3' - 4" |
| 7170-7180 Thermal French 40x96 Ovolo Flat Panel | Thermal French TDL - Single Lite - Insulated Glazed | 8' - 0" | 7170-7180 | 4 | 1 | 8' - 2" | 3' - 8" | 3' - 4" |
| 7170-7180 Thermal French 42x80 Ovolo Flat Panel | Thermal French TDL - Single Lite - Insulated Glazed | 6' - 8" | 7170-7180 | 4 | 1 | 6' - 10" | 3' - 10" | 3' - 6" |
| 7170-7180 Thermal French 42x84 Ovolo Flat Panel | Thermal French TDL - Single Lite - Insulated Glazed | 7' - 0" | 7170-7180 | 4 | 1 | 7' - 2" | 3' - 10" | 3' - 6" |
| 7170-7180 Thermal French 42x96 Ovolo Flat Panel | Thermal French TDL - Single Lite - Insulated Glazed | 8' - 0" | 7170-7180 | 4 | 1 | 8' - 2" | 3' - 10" | 3' - 6" |
| 7171-7181 Thermal French 30x80 Ovolo Flat Panel | Thermal French TDL - Single Lite - Insulated Glazed | 6' - 8" | 7171-7181 | 0 | 0 | 6' - 10" | 2' - 10" | 2' - 6" |
| 7171-7181 Thermal French 30x84 Ovolo Flat Panel | Thermal French TDL - Single Lite - Insulated Glazed | 7' - 0" | 7171-7181 | 0 | 0 | 7' - 2" | 2' - 10" | 2' - 6" |
| 7171-7181 Thermal French 30x96 Ovolo Flat Panel | Thermal French TDL - Single Lite - Insulated Glazed | 8' - 0" | 7171-7181 | 0 | 0 | 8' - 2" | 2' - 10" | 2' - 6" |
| 7171-7181 Thermal French 32x80 Ovolo Flat Panel | Thermal French TDL - Single Lite - Insulated Glazed | 6' - 8" | 7171-7181 | 0 | 0 | 6' - 10" | 3' - 0" | 2' - 8" |
| 7171-7181 Thermal French 32x84 Ovolo Flat Panel | Thermal French TDL - Single Lite - Insulated Glazed | 7' - 0" | 7171-7181 | 0 | 0 | 7' - 2" | 3' - 0" | 2' - 8" |
| 7171-7181 Thermal French 32x96 Ovolo Flat Panel | Thermal French TDL - Single Lite - Insulated Glazed | 8' - 0" | 7171-7181 | 0 | 0 | 8' - 2" | 3' - 0" | 2' - 8" |
| 7171-7181 Thermal French 34x80 Ovolo Flat Panel | Thermal French TDL - Single Lite - Insulated Glazed | 6' - 8" | 7171-7181 | 0 | 0 | 6' - 10" | 3' - 2" | 2' - 10" |
| 7171-7181 Thermal French 34x84 Ovolo Flat Panel | Thermal French TDL - Single Lite - Insulated Glazed | 7' - 0" | 7171-7181 | 0 | 0 | 7' - 2" | 3' - 2" | 2' - 10" |
| 7171-7181 Thermal French 34x96 Ovolo Flat Panel | Thermal French TDL - Single Lite - Insulated Glazed | 8' - 0" | 7171-7181 | 0 | 0 | 8' - 2" | 3' - 2" | 2' - 10" |
| 7171-7181 Thermal French 36x80 Ovolo Flat Panel | Thermal French TDL - Single Lite - Insulated Glazed | 6' - 8" | 7171-7181 | 0 | 0 | 6' - 10" | 3' - 4" | 3' - 0" |
| 7171-7181 Thermal French 36x84 Ovolo Flat Panel | Thermal French TDL - Single Lite - Insulated Glazed | 7' - 0" | 7171-7181 | 0 | 0 | 7' - 2" | 3' - 4" | 3' - 0" |
| 7171-7181 Thermal French 36x96 Ovolo Flat Panel | Thermal French TDL - Single Lite - Insulated Glazed | 8' - 0" | 7171-7181 | 0 | 0 | 8' - 2" | 3' - 4" | 3' - 0" |
| 7171-7181 Thermal French 38x80 Ovolo Flat Panel | Thermal French TDL - Single Lite - Insulated Glazed | 6' - 8" | 7171-7181 | 0 | 0 | 6' - 10" | 3' - 6" | 3' - 2" |
| 7171-7181 Thermal French 38x84 Ovolo Flat Panel | Thermal French TDL - Single Lite - Insulated Glazed | 7' - 0" | 7171-7181 | 0 | 0 | 7' - 2" | 3' - 6" | 3' - 2" |
| 7171-7181 Thermal French 38x96 Ovolo Flat Panel | Thermal French TDL - Single Lite - Insulated Glazed | 8' - 0" | 7171-7181 | 0 | 0 | 8' - 2" | 3' - 6" | 3' - 2" |
| 7171-7181 Thermal French 40x80 Ovolo Flat Panel | Thermal French TDL - Single Lite - Insulated Glazed | 6' - 8" | 7171-7181 | 0 | 0 | 6' - 10" | 3' - 8" | 3' - 4" |
| 7171-7181 Thermal French 40x84 Ovolo Flat Panel | Thermal French TDL - Single Lite - Insulated Glazed | 7' - 0" | 7171-7181 | 0 | 0 | 7' - 2" | 3' - 8" | 3' - 4" |
| 7171-7181 Thermal French 40x96 Ovolo Flat Panel | Thermal French TDL - Single Lite - Insulated Glazed | 8' - 0" | 7171-7181 | 0 | 0 | 8' - 2" | 3' - 8" | 3' - 4" |
| 7171-7181 Thermal French 42x80 Ovolo Flat Panel | Thermal French TDL - Single Lite - Insulated Glazed | 6' - 8" | 7171-7181 | 0 | 0 | 6' - 10" | 3' - 10" | 3' - 6" |
| 7171-7181 Thermal French 42x84 Ovolo Flat Panel | Thermal French TDL - Single Lite - Insulated Glazed | 7' - 0" | 7171-7181 | 0 | 0 | 7' - 2" | 3' - 10" | 3' - 6" |
| 7171-7181 Thermal French 42x96 Ovolo Flat Panel | Thermal French TDL - Single Lite - Insulated Glazed | 8' - 0" | 7171-7181 | 0 | 0 | 8' - 2" | 3' - 10" | 3' - 6" |
| 7176-7186 Thermal French 30x80 Ovolo Flat Panel | Thermal French TDL - Six Lite | 6' - 8" | 7176-7186 | 2 | 1 | 6' - 10" | 2' - 10" | 2' - 6" |
| 7176-7186 Thermal French 30x84 Ovolo Flat Panel | Thermal French TDL - Six Lite | 7' - 0" | 7176-7186 | 2 | 1 | 7' - 2" | 2' - 10" | 2' - 6" |
| 7176-7186 Thermal French 30x96 Ovolo Flat Panel | Thermal French TDL - Six Lite | 8' - 0" | 7176-7186 | 2 | 1 | 8' - 2" | 2' - 10" | 2' - 6" |
| 7176-7186 Thermal French 32x80 Ovolo Flat Panel | Thermal French TDL - Six Lite | 6' - 8" | 7176-7186 | 2 | 1 | 6' - 10" | 3' - 0" | 2' - 8" |
| 7176-7186 Thermal French 32x84 Ovolo Flat Panel | Thermal French TDL - Six Lite | 7' - 0" | 7176-7186 | 2 | 1 | 7' - 2" | 3' - 0" | 2' - 8" |
| 7176-7186 Thermal French 32x96 Ovolo Flat Panel | Thermal French TDL - Six Lite | 8' - 0" | 7176-7186 | 2 | 1 | 8' - 2" | 3' - 0" | 2' - 8" |
| 7176-7186 Thermal French 34x80 Ovolo Flat Panel | Thermal French TDL - Six Lite | 6' - 8" | 7176-7186 | 2 | 1 | 6' - 10" | 3' - 2" | 2' - 10" |
| 7176-7186 Thermal French 34x84 Ovolo Flat Panel | Thermal French TDL - Six Lite | 7' - 0" | 7176-7186 | 2 | 1 | 7' - 2" | 3' - 2" | 2' - 10" |
| 7176-7186 Thermal French 34x96 Ovolo Flat Panel | Thermal French TDL - Six Lite | 8' - 0" | 7176-7186 | 2 | 1 | 8' - 2" | 3' - 2" | 2' - 10" |
| 7176-7186 Thermal French 36x80 Ovolo Flat Panel | Thermal French TDL - Six Lite | 6' - 8" | 7176-7186 | 2 | 1 | 6' - 10" | 3' - 4" | 3' - 0" |
| 7176-7186 Thermal French 36x84 Ovolo Flat Panel | Thermal French TDL - Six Lite | 7' - 0" | 7176-7186 | 2 | 1 | 7' - 2" | 3' - 4" | 3' - 0" |
| 7176-7186 Thermal French 36x96 Ovolo Flat Panel | Thermal French TDL - Six Lite | 8' - 0" | 7176-7186 | 2 | 1 | 8' - 2" | 3' - 4" | 3' - 0" |
| 7176-7186 Thermal French 38x80 Ovolo Flat Panel | Thermal French TDL - Six Lite | 6' - 8" | 7176-7186 | 2 | 1 | 6' - 10" | 3' - 6" | 3' - 2" |
| 7176-7186 Thermal French 38x84 Ovolo Flat Panel | Thermal French TDL - Six Lite | 7' - 0" | 7176-7186 | 2 | 1 | 7' - 2" | 3' - 6" | 3' - 2" |
| 7176-7186 Thermal French 38x96 Ovolo Flat Panel | Thermal French TDL - Six Lite | 8' - 0" | 7176-7186 | 2 | 1 | 8' - 2" | 3' - 6" | 3' - 2" |
| 7176-7186 Thermal French 40x80 Ovolo Flat Panel | Thermal French TDL - Six Lite | 6' - 8" | 7176-7186 | 2 | 1 | 6' - 10" | 3' - 8" | 3' - 4" |
| 7176-7186 Thermal French 40x84 Ovolo Flat Panel | Thermal French TDL - Six Lite | 7' - 0" | 7176-7186 | 2 | 1 | 7' - 2" | 3' - 8" | 3' - 4" |
| 7176-7186 Thermal French 40x96 Ovolo Flat Panel | Thermal French TDL - Six Lite | 8' - 0" | 7176-7186 | 2 | 1 | 8' - 2" | 3' - 8" | 3' - 4" |
| 7176-7186 Thermal French 42x80 Ovolo Flat Panel | Thermal French TDL - Six Lite | 6' - 8" | 7176-7186 | 2 | 1 | 6' - 10" | 3' - 10" | 3' - 6" |
| 7176-7186 Thermal French 42x84 Ovolo Flat Panel | Thermal French TDL - Six Lite | 7' - 0" | 7176-7186 | 2 | 1 | 7' - 2" | 3' - 10" | 3' - 6" |
| 7176-7186 Thermal French 42x96 Ovolo Flat Panel | Thermal French TDL - Six Lite | 8' - 0" | 7176-7186 | 2 | 1 | 8' - 2" | 3' - 10" | 3' - 6" |
| 7178-7188 Thermal French 30x80 Ovolo Flat Panel | Thermal French TDL - Eight Lite | 6' - 8" | 7178-7188 | 3 | 1 | 6' - 10" | 2' - 10" | 2' - 6" |
| 7178-7188 Thermal French 30x84 Ovolo Flat Panel | Thermal French TDL - Eight Lite | 7' - 0" | 7178-7188 | 3 | 1 | 7' - 2" | 2' - 10" | 2' - 6" |
| 7178-7188 Thermal French 30x96 Ovolo Flat Panel | Thermal French TDL - Eight Lite | 8' - 0" | 7178-7188 | 3 | 1 | 8' - 2" | 2' - 10" | 2' - 6" |
| 7178-7188 Thermal French 32x80 Ovolo Flat Panel | Thermal French TDL - Eight Lite | 6' - 8" | 7178-7188 | 3 | 1 | 6' - 10" | 3' - 0" | 2' - 8" |
| 7178-7188 Thermal French 32x84 Ovolo Flat Panel | Thermal French TDL - Eight Lite | 7' - 0" | 7178-7188 | 3 | 1 | 7' - 2" | 3' - 0" | 2' - 8" |
| 7178-7188 Thermal French 32x96 Ovolo Flat Panel | Thermal French TDL - Eight Lite | 8' - 0" | 7178-7188 | 3 | 1 | 8' - 2" | 3' - 0" | 2' - 8" |
| 7178-7188 Thermal French 34x80 Ovolo Flat Panel | Thermal French TDL - Eight Lite | 6' - 8" | 7178-7188 | 3 | 1 | 6' - 10" | 3' - 2" | 2' - 10" |
| 7178-7188 Thermal French 34x84 Ovolo Flat Panel | Thermal French TDL - Eight Lite | 7' - 0" | 7178-7188 | 3 | 1 | 7' - 2" | 3' - 2" | 2' - 10" |
| 7178-7188 Thermal French 34x96 Ovolo Flat Panel | Thermal French TDL - Eight Lite | 8' - 0" | 7178-7188 | 3 | 1 | 8' - 2" | 3' - 2" | 2' - 10" |
| 7178-7188 Thermal French 36x80 Ovolo Flat Panel | Thermal French TDL - Eight Lite | 6' - 8" | 7178-7188 | 3 | 1 | 6' - 10" | 3' - 4" | 3' - 0" |
| 7178-7188 Thermal French 36x84 Ovolo Flat Panel | Thermal French TDL - Eight Lite | 7' - 0" | 7178-7188 | 3 | 1 | 7' - 2" | 3' - 4" | 3' - 0" |
| 7178-7188 Thermal French 36x96 Ovolo Flat Panel | Thermal French TDL - Eight Lite | 8' - 0" | 7178-7188 | 3 | 1 | 8' - 2" | 3' - 4" | 3' - 0" |
| 7178-7188 Thermal French 38x80 Ovolo Flat Panel | Thermal French TDL - Eight Lite | 6' - 8" | 7178-7188 | 3 | 1 | 6' - 10" | 3' - 6" | 3' - 2" |
| 7178-7188 Thermal French 38x84 Ovolo Flat Panel | Thermal French TDL - Eight Lite | 7' - 0" | 7178-7188 | 3 | 1 | 7' - 2" | 3' - 6" | 3' - 2" |
| 7178-7188 Thermal French 38x96 Ovolo Flat Panel | Thermal French TDL - Eight Lite | 8' - 0" | 7178-7188 | 3 | 1 | 8' - 2" | 3' - 6" | 3' - 2" |
| 7178-7188 Thermal French 40x80 Ovolo Flat Panel | Thermal French TDL - Eight Lite | 6' - 8" | 7178-7188 | 3 | 1 | 6' - 10" | 3' - 8" | 3' - 4" |
| 7178-7188 Thermal French 40x84 Ovolo Flat Panel | Thermal French TDL - Eight Lite | 7' - 0" | 7178-7188 | 3 | 1 | 7' - 2" | 3' - 8" | 3' - 4" |
| 7178-7188 Thermal French 40x96 Ovolo Flat Panel | Thermal French TDL - Eight Lite | 8' - 0" | 7178-7188 | 3 | 1 | 8' - 2" | 3' - 8" | 3' - 4" |
| 7178-7188 Thermal French 42x80 Ovolo Flat Panel | Thermal French TDL - Eight Lite | 6' - 8" | 7178-7188 | 3 | 1 | 6' - 10" | 3' - 10" | 3' - 6" |
| 7178-7188 Thermal French 42x84 Ovolo Flat Panel | Thermal French TDL - Eight Lite | 7' - 0" | 7178-7188 | 3 | 1 | 7' - 2" | 3' - 10" | 3' - 6" |
| 7178-7188 Thermal French 42x96 Ovolo Flat Panel | Thermal French TDL - Eight Lite | 8' - 0" | 7178-7188 | 3 | 1 | 8' - 2" | 3' - 10" | 3' - 6" |

## geometry (parser evidence)
native form markers: Blend x30, Sweep x16
no freeform markers — native parametric forms only
